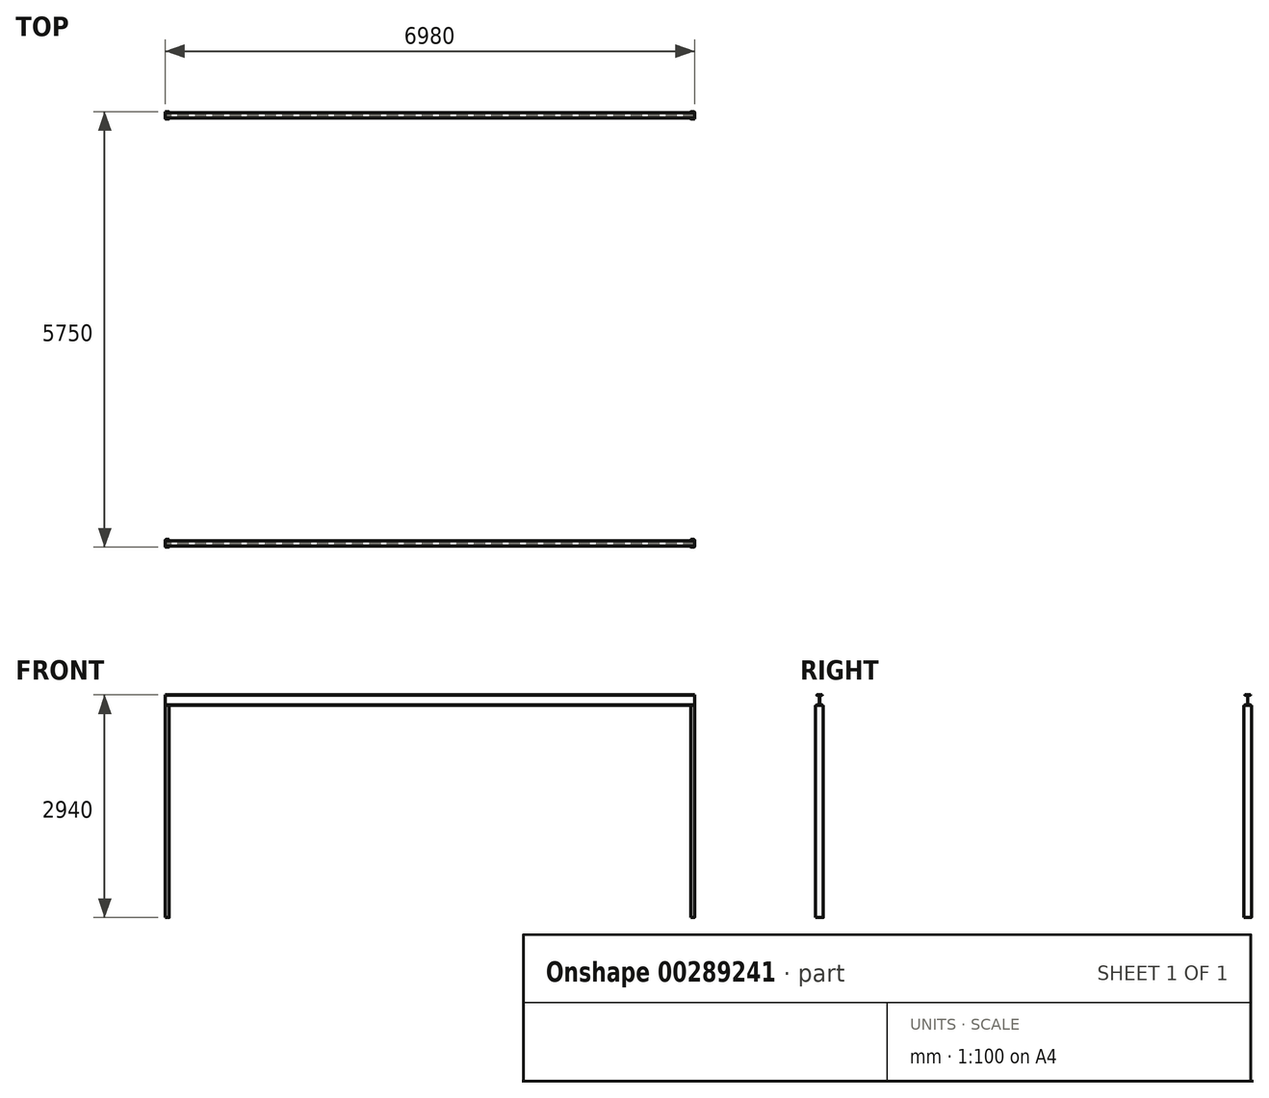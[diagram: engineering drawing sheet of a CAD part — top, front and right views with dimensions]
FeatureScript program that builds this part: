
annotation { "Feature Type Name" : "Feature", "Feature Type Description" : "" }
export const myFeature = defineFeature(function(context is Context, id is Id, definition is map)
    precondition{}
    {
        {
            var Q0;
            Q0=qCreatedBy(makeId("Top.planeOp"),FACE);
            var sketch = newSketch(context, id + "F0", { "sketchPlane" : qUnion([Q0])});
            skLineSegment(sketch, "E0.bottom", {"start": v(-3055.89, 5361.75) * mm, "end": v(4444.11, 5361.75) * mm});
            skLineSegment(sketch, "E0.top", {"start": v(-3055.89, -4138.25) * mm, "end": v(4444.11, -4138.25) * mm});
            skLineSegment(sketch, "E0.left", {"start": v(-3055.89, 5361.75) * mm, "end": v(-3055.89, -4138.25) * mm});
            skLineSegment(sketch, "E0.right", {"start": v(4444.11, 5361.75) * mm, "end": v(4444.11, -4138.25) * mm});
            skLineSegment(sketch, "E1.bottom", {"start": v(-1742.64, 710.32) * mm, "end": v(7.36, 710.32) * mm, "construction": true});
            skLineSegment(sketch, "E1.top", {"start": v(-1742.64, -3489.68) * mm, "end": v(7.36, -3489.68) * mm, "construction": true});
            skLineSegment(sketch, "E1.left", {"start": v(-1742.64, 710.32) * mm, "end": v(-1742.64, -3489.68) * mm, "construction": true});
            skLineSegment(sketch, "E1.right", {"start": v(7.36, 710.32) * mm, "end": v(7.36, -3489.68) * mm, "construction": true});
            skLineSegment(sketch, "E2", {"start": v(4444.11, 3111.75) * mm, "end": v(-3055.89, 3111.75) * mm, "construction": true});
            skSolve(sketch);
        }
        {
            var Q0;
            Q0=makeQuery(id+"F0.imprint","IMPRINT",FACE,{"disambiguationData":[TD([[makeQuery(id+"F0.imprint","IMPRINT",EDGE,{"derivedFrom":sQuery(id+"F0.wireOp",EDGE,"E0.bottom")}),-1.0]])]});
            var sketch = newSketch(context, id + "F1", { "sketchPlane" : qUnion([Q0])});
            skLineSegment(sketch, "E3.bottom", {"start": v(-2790.89, 2611.75) * mm, "end": v(-2750.89, 2611.75) * mm});
            skLineSegment(sketch, "E3.top", {"start": v(-2790.89, 2511.75) * mm, "end": v(-2750.89, 2511.75) * mm});
            skLineSegment(sketch, "E3.left", {"start": v(-2795.89, 2606.75) * mm, "end": v(-2795.89, 2516.75) * mm});
            skLineSegment(sketch, "E3.right", {"start": v(-2745.89, 2606.75) * mm, "end": v(-2745.89, 2516.75) * mm});
            skPoint(sketch, "E4.visualSharp", {"position": v(-2795.89, 2611.75) * mm});
            skArc(sketch, "E4.filletArc", {"start": v(-2790.89, 2611.75) * mm, "mid": v(-2794.42, 2610.28) * mm, "end": v(-2795.89, 2606.75) * mm});
            skPoint(sketch, "E5.visualSharp", {"position": v(-2745.89, 2611.75) * mm});
            skArc(sketch, "E5.filletArc", {"start": v(-2745.89, 2606.75) * mm, "mid": v(-2747.35, 2610.28) * mm, "end": v(-2750.89, 2611.75) * mm});
            skPoint(sketch, "E6.visualSharp", {"position": v(-2795.89, 2511.75) * mm});
            skArc(sketch, "E6.filletArc", {"start": v(-2795.89, 2516.75) * mm, "mid": v(-2794.42, 2513.2) * mm, "end": v(-2790.89, 2511.75) * mm});
            skPoint(sketch, "E7.visualSharp", {"position": v(-2745.89, 2511.75) * mm});
            skArc(sketch, "E7.filletArc", {"start": v(-2750.89, 2511.75) * mm, "mid": v(-2747.35, 2513.2) * mm, "end": v(-2745.89, 2516.75) * mm});
            skLineSegment(sketch, "E8", {"start": v(694.11, -6016.74) * mm, "end": v(694.11, 3131.84) * mm, "construction": true});
            skLineSegment(sketch, "E9", {"start": v(-4490.18, -263.25) * mm, "end": v(9245.09, -263.25) * mm, "construction": true});
            skArc(sketch, "E10.MirrorCS", {"start": v(-2795.89, -3043.25) * mm, "mid": v(-2794.42, -3039.72) * mm, "end": v(-2790.89, -3038.25) * mm});
            skArc(sketch, "E11.MirrorCS", {"start": v(-2790.89, -3138.25) * mm, "mid": v(-2794.42, -3136.8) * mm, "end": v(-2795.89, -3133.25) * mm});
            skLineSegment(sketch, "E12.MirrorCS", {"start": v(-2790.89, -3038.25) * mm, "end": v(-2750.89, -3038.25) * mm});
            skLineSegment(sketch, "E13.MirrorCS", {"start": v(-2790.89, -3138.25) * mm, "end": v(-2750.89, -3138.25) * mm});
            skArc(sketch, "E14.MirrorCS", {"start": v(-2750.89, -3038.25) * mm, "mid": v(-2747.35, -3039.72) * mm, "end": v(-2745.89, -3043.25) * mm});
            skArc(sketch, "E15.MirrorCS", {"start": v(-2745.89, -3133.25) * mm, "mid": v(-2747.35, -3136.8) * mm, "end": v(-2750.89, -3138.25) * mm});
            skPoint(sketch, "E16.MirrorP", {"position": v(-2745.89, -3038.25) * mm});
            skLineSegment(sketch, "E17.MirrorCS", {"start": v(-2795.89, -3133.25) * mm, "end": v(-2795.89, -3043.25) * mm});
            skLineSegment(sketch, "E18.MirrorCS", {"start": v(-2745.89, -3133.25) * mm, "end": v(-2745.89, -3043.25) * mm});
            skPoint(sketch, "E19.MirrorP", {"position": v(-2795.89, -3038.25) * mm});
            skPoint(sketch, "E20.MirrorP", {"position": v(-2745.89, -3138.25) * mm});
            skPoint(sketch, "E21.MirrorP", {"position": v(-2795.89, -3138.25) * mm});
            skArc(sketch, "E22.MirrorCS", {"start": v(4139.11, -3038.25) * mm, "mid": v(4135.58, -3039.72) * mm, "end": v(4134.11, -3043.25) * mm});
            skLineSegment(sketch, "E23.MirrorCS", {"start": v(4184.11, -3133.25) * mm, "end": v(4184.11, -3043.25) * mm});
            skLineSegment(sketch, "E24.MirrorCS", {"start": v(4179.11, -3138.25) * mm, "end": v(4139.11, -3138.25) * mm});
            skArc(sketch, "E25.MirrorCS", {"start": v(4134.11, -3133.25) * mm, "mid": v(4135.58, -3136.8) * mm, "end": v(4139.11, -3138.25) * mm});
            skArc(sketch, "E26.MirrorCS", {"start": v(4184.11, -3043.25) * mm, "mid": v(4182.65, -3039.72) * mm, "end": v(4179.11, -3038.25) * mm});
            skArc(sketch, "E27.MirrorCS", {"start": v(4179.11, -3138.25) * mm, "mid": v(4182.65, -3136.8) * mm, "end": v(4184.11, -3133.25) * mm});
            skLineSegment(sketch, "E28.MirrorCS", {"start": v(4134.11, -3133.25) * mm, "end": v(4134.11, -3043.25) * mm});
            skLineSegment(sketch, "E29.MirrorCS", {"start": v(4179.11, -3038.25) * mm, "end": v(4139.11, -3038.25) * mm});
            skLineSegment(sketch, "E30.MirrorCS", {"start": v(4179.11, 2511.75) * mm, "end": v(4139.11, 2511.75) * mm});
            skLineSegment(sketch, "E31.MirrorCS", {"start": v(4179.11, 2611.75) * mm, "end": v(4139.11, 2611.75) * mm});
            skLineSegment(sketch, "E32.MirrorCS", {"start": v(4134.11, 2606.75) * mm, "end": v(4134.11, 2516.75) * mm});
            skLineSegment(sketch, "E33.MirrorCS", {"start": v(4184.11, 2606.75) * mm, "end": v(4184.11, 2516.75) * mm});
            skArc(sketch, "E34.MirrorCS", {"start": v(4179.11, 2611.75) * mm, "mid": v(4182.65, 2610.28) * mm, "end": v(4184.11, 2606.75) * mm});
            skArc(sketch, "E35.MirrorCS", {"start": v(4134.11, 2606.75) * mm, "mid": v(4135.58, 2610.28) * mm, "end": v(4139.11, 2611.75) * mm});
            skArc(sketch, "E36.MirrorCS", {"start": v(4184.11, 2516.75) * mm, "mid": v(4182.65, 2513.2) * mm, "end": v(4179.11, 2511.75) * mm});
            skArc(sketch, "E37.MirrorCS", {"start": v(4139.11, 2511.75) * mm, "mid": v(4135.58, 2513.2) * mm, "end": v(4134.11, 2516.75) * mm});
            skPoint(sketch, "E38.MirrorP", {"position": v(4134.11, 2511.75) * mm});
            skPoint(sketch, "E39.MirrorP", {"position": v(4184.11, 2611.75) * mm});
            skPoint(sketch, "E40.MirrorP", {"position": v(4184.11, 2511.75) * mm});
            skPoint(sketch, "E41.MirrorP", {"position": v(4134.11, 2611.75) * mm});
            skPoint(sketch, "E42.MirrorP", {"position": v(4134.11, -3138.25) * mm});
            skPoint(sketch, "E43.MirrorP", {"position": v(4134.11, -3038.25) * mm});
            skPoint(sketch, "E44.MirrorP", {"position": v(4184.11, -3138.25) * mm});
            skPoint(sketch, "E45.MirrorP", {"position": v(4184.11, -3038.25) * mm});
            skSolve(sketch);
        }
        {
            var Q0;
            Q0 = qSketchRegion(id + "F1", true);
            extrude(context, id + "F2", {"entities" : qUnion([Q0]), "depth" : 2800 * mm});
        }
        {
            var Q0;
            Q0=makeQuery(id+"F2.opExtrude","SWEPT_FACE",FACE,{"disambiguationData":[OSD([sQuery(id+"F1.wireOp",EDGE,"E17.MirrorCS")])]});
            var sketch = newSketch(context, id + "F3", { "sketchPlane" : qUnion([Q0])});
            skLineSegment(sketch, "E46", {"start": v(3088.25, 2851.79) * mm, "end": v(3088.25, 2793.23) * mm, "construction": true});
            skLineSegment(sketch, "E47", {"start": v(3053.75, 2800) * mm, "end": v(3088.25, 2800) * mm});
            skLineSegment(sketch, "E48", {"start": v(3051.75, 2802) * mm, "end": v(3051.75, 2804.9) * mm});
            skLineSegment(sketch, "E49", {"start": v(3053.75, 2806.9) * mm, "end": v(3083.9, 2806.9) * mm});
            skLineSegment(sketch, "E50", {"start": v(3085.9, 2808.9) * mm, "end": v(3085.9, 2931.1) * mm});
            skLineSegment(sketch, "E51", {"start": v(3083.9, 2933.1) * mm, "end": v(3053.75, 2933.1) * mm});
            skLineSegment(sketch, "E52", {"start": v(3051.75, 2935.1) * mm, "end": v(3051.75, 2938) * mm});
            skLineSegment(sketch, "E53", {"start": v(3053.75, 2940) * mm, "end": v(3088.25, 2940) * mm});
            skLineSegment(sketch, "E54.MirrorCS", {"start": v(3122.75, 2940) * mm, "end": v(3088.25, 2940) * mm});
            skLineSegment(sketch, "E55.MirrorCS", {"start": v(3124.75, 2935.1) * mm, "end": v(3124.75, 2938) * mm});
            skLineSegment(sketch, "E56.MirrorCS", {"start": v(3092.6, 2933.1) * mm, "end": v(3122.75, 2933.1) * mm});
            skLineSegment(sketch, "E57.MirrorCS", {"start": v(3090.6, 2808.9) * mm, "end": v(3090.6, 2931.1) * mm});
            skLineSegment(sketch, "E58.MirrorCS", {"start": v(3122.75, 2806.9) * mm, "end": v(3092.6, 2806.9) * mm});
            skLineSegment(sketch, "E59.MirrorCS", {"start": v(3122.75, 2800) * mm, "end": v(3088.25, 2800) * mm});
            skLineSegment(sketch, "E60.MirrorCS", {"start": v(3124.75, 2802) * mm, "end": v(3124.75, 2804.9) * mm});
            skPoint(sketch, "E61.visualSharp", {"position": v(3051.75, 2800) * mm});
            skArc(sketch, "E61.filletArc", {"start": v(3051.75, 2802) * mm, "mid": v(3052.34, 2800.59) * mm, "end": v(3053.75, 2800) * mm});
            skPoint(sketch, "E62.visualSharp", {"position": v(3051.75, 2806.9) * mm});
            skArc(sketch, "E62.filletArc", {"start": v(3053.75, 2806.9) * mm, "mid": v(3052.34, 2806.31) * mm, "end": v(3051.75, 2804.9) * mm});
            skPoint(sketch, "E63.visualSharp", {"position": v(3124.75, 2806.9) * mm});
            skArc(sketch, "E63.filletArc", {"start": v(3124.75, 2804.9) * mm, "mid": v(3124.17, 2806.31) * mm, "end": v(3122.75, 2806.9) * mm});
            skPoint(sketch, "E64.visualSharp", {"position": v(3124.75, 2800) * mm});
            skArc(sketch, "E64.filletArc", {"start": v(3122.75, 2800) * mm, "mid": v(3124.17, 2800.59) * mm, "end": v(3124.75, 2802) * mm});
            skPoint(sketch, "E65.visualSharp", {"position": v(3090.6, 2806.9) * mm});
            skArc(sketch, "E65.filletArc", {"start": v(3090.6, 2808.9) * mm, "mid": v(3091.2, 2807.49) * mm, "end": v(3092.6, 2806.9) * mm});
            skPoint(sketch, "E66.visualSharp", {"position": v(3085.9, 2806.9) * mm});
            skArc(sketch, "E66.filletArc", {"start": v(3083.9, 2806.9) * mm, "mid": v(3085.32, 2807.49) * mm, "end": v(3085.9, 2808.9) * mm});
            skPoint(sketch, "E67.visualSharp", {"position": v(3085.9, 2933.1) * mm});
            skArc(sketch, "E67.filletArc", {"start": v(3085.9, 2931.1) * mm, "mid": v(3085.32, 2932.51) * mm, "end": v(3083.9, 2933.1) * mm});
            skPoint(sketch, "E68.visualSharp", {"position": v(3090.6, 2933.1) * mm});
            skArc(sketch, "E68.filletArc", {"start": v(3092.6, 2933.1) * mm, "mid": v(3091.2, 2932.51) * mm, "end": v(3090.6, 2931.1) * mm});
            skPoint(sketch, "E69.visualSharp", {"position": v(3051.75, 2933.1) * mm});
            skArc(sketch, "E69.filletArc", {"start": v(3051.75, 2935.1) * mm, "mid": v(3052.34, 2933.69) * mm, "end": v(3053.75, 2933.1) * mm});
            skPoint(sketch, "E70.visualSharp", {"position": v(3051.75, 2940) * mm});
            skArc(sketch, "E70.filletArc", {"start": v(3053.75, 2940) * mm, "mid": v(3052.34, 2939.41) * mm, "end": v(3051.75, 2938) * mm});
            skPoint(sketch, "E71.visualSharp", {"position": v(3124.75, 2940) * mm});
            skArc(sketch, "E71.filletArc", {"start": v(3124.75, 2938) * mm, "mid": v(3124.17, 2939.41) * mm, "end": v(3122.75, 2940) * mm});
            skPoint(sketch, "E72.visualSharp", {"position": v(3124.75, 2933.1) * mm});
            skArc(sketch, "E72.filletArc", {"start": v(3122.75, 2933.1) * mm, "mid": v(3124.17, 2933.69) * mm, "end": v(3124.75, 2935.1) * mm});
            skLineSegment(sketch, "E73", {"start": v(263.25, 3538.43) * mm, "end": v(263.25, -738.72) * mm, "construction": true});
            skArc(sketch, "E74.MirrorCS", {"start": v(3122.75, 2806.9) * mm, "mid": v(3124.17, 2806.31) * mm, "end": v(3124.75, 2804.9) * mm});
            skArc(sketch, "E75.MirrorCS", {"start": v(3124.75, 2802) * mm, "mid": v(3124.17, 2800.59) * mm, "end": v(3122.75, 2800) * mm});
            skArc(sketch, "E76.MirrorCS", {"start": v(3051.75, 2938) * mm, "mid": v(3052.34, 2939.41) * mm, "end": v(3053.75, 2940) * mm});
            skArc(sketch, "E77.MirrorCS", {"start": v(3122.75, 2940) * mm, "mid": v(3124.17, 2939.41) * mm, "end": v(3124.75, 2938) * mm});
            skArc(sketch, "E78.MirrorCS", {"start": v(3090.6, 2931.1) * mm, "mid": v(3091.2, 2932.51) * mm, "end": v(3092.6, 2933.1) * mm});
            skArc(sketch, "E79.MirrorCS", {"start": v(3051.75, 2804.9) * mm, "mid": v(3052.34, 2806.31) * mm, "end": v(3053.75, 2806.9) * mm});
            skArc(sketch, "E80.MirrorCS", {"start": v(3124.75, 2935.1) * mm, "mid": v(3124.17, 2933.69) * mm, "end": v(3122.75, 2933.1) * mm});
            skArc(sketch, "E81.MirrorCS", {"start": v(3053.75, 2800) * mm, "mid": v(3052.34, 2800.59) * mm, "end": v(3051.75, 2802) * mm});
            skArc(sketch, "E82.MirrorCS", {"start": v(3053.75, 2933.1) * mm, "mid": v(3052.34, 2933.69) * mm, "end": v(3051.75, 2935.1) * mm});
            skArc(sketch, "E83.MirrorCS", {"start": v(3083.9, 2933.1) * mm, "mid": v(3085.32, 2932.51) * mm, "end": v(3085.9, 2931.1) * mm});
            skArc(sketch, "E84.MirrorCS", {"start": v(3085.9, 2808.9) * mm, "mid": v(3085.32, 2807.49) * mm, "end": v(3083.9, 2806.9) * mm});
            skArc(sketch, "E85.MirrorCS", {"start": v(3092.6, 2806.9) * mm, "mid": v(3091.2, 2807.49) * mm, "end": v(3090.6, 2808.9) * mm});
            skSolve(sketch);
        }
        {
            var Q0;
            Q0 = qSketchRegion(id + "F3", true);
            var Q1;
            Q1=makeQuery(id+"F2.opExtrude","SWEPT_FACE",FACE,{"disambiguationData":[OSD([sQuery(id+"F1.wireOp",EDGE,"E23.MirrorCS")])]});
            extrude(context, id + "F4", {"entities" : qUnion([Q0]), "endBound" : BoundingType.UP_TO_SURFACE, "oppositeDirection" : true, "endBoundEntityFace" : qUnion([Q1]), "depth" : 25 * mm});
        }
        {
            var Q0;
            Q0=makeQuery(id+"F2.opExtrude","SWEPT_FACE",FACE,{"disambiguationData":[OSD([sQuery(id+"F1.wireOp",EDGE,"E3.top")])]});
            var Q1;
            Q1=makeQuery(id+"F2.opExtrude","SWEPT_FACE",FACE,{"disambiguationData":[OSD([sQuery(id+"F1.wireOp",EDGE,"E12.MirrorCS")])]});
            cPlane(context, id + "F5", {"entities" : qUnion([Q0, Q1]), "cplaneType" : CPlaneType.MID_PLANE, "offset" : 25 * mm, "width" : 150 * mm, "height" : 150 * mm});
        }
        {
            var Q0;
            Q0=makeQuery(id+"F4.opExtrude","SWEPT_BODY",BODY,{"disambiguationData":[OSD([sQuery(id+"F3.wireOp",EDGE,"E71.filletArc"),sQuery(id+"F3.wireOp",EDGE,"E55.MirrorCS"),sQuery(id+"F3.wireOp",EDGE,"E79.MirrorCS"),sQuery(id+"F3.wireOp",EDGE,"E61.filletArc"),sQuery(id+"F3.wireOp",EDGE,"E80.MirrorCS"),sQuery(id+"F3.wireOp",EDGE,"E48"),sQuery(id+"F3.wireOp",EDGE,"E56.MirrorCS"),sQuery(id+"F3.wireOp",EDGE,"E78.MirrorCS"),sQuery(id+"F3.wireOp",EDGE,"E83.MirrorCS"),sQuery(id+"F3.wireOp",EDGE,"E54.MirrorCS"),sQuery(id+"F3.wireOp",EDGE,"E60.MirrorCS"),sQuery(id+"F3.wireOp",EDGE,"E64.filletArc"),sQuery(id+"F3.wireOp",EDGE,"E63.filletArc"),sQuery(id+"F3.wireOp",EDGE,"E84.MirrorCS"),sQuery(id+"F3.wireOp",EDGE,"E59.MirrorCS"),sQuery(id+"F3.wireOp",EDGE,"E58.MirrorCS"),sQuery(id+"F3.wireOp",EDGE,"E47"),sQuery(id+"F3.wireOp",EDGE,"E49"),sQuery(id+"F3.wireOp",EDGE,"E65.filletArc"),sQuery(id+"F3.wireOp",EDGE,"E52"),sQuery(id+"F3.wireOp",EDGE,"E69.filletArc"),sQuery(id+"F3.wireOp",EDGE,"E53"),sQuery(id+"F3.wireOp",EDGE,"E76.MirrorCS"),sQuery(id+"F3.wireOp",EDGE,"E51"),sQuery(id+"F3.wireOp",EDGE,"E57.MirrorCS"),sQuery(id+"F3.wireOp",EDGE,"E50")])]});
            var Q1;
            Q1=qCreatedBy(id+"F5.planeOp",FACE);
            mirror(context, id + "F6", {"entities" : qUnion([Q0]), "mirrorPlane" : qUnion([Q1])});
        }
    });
